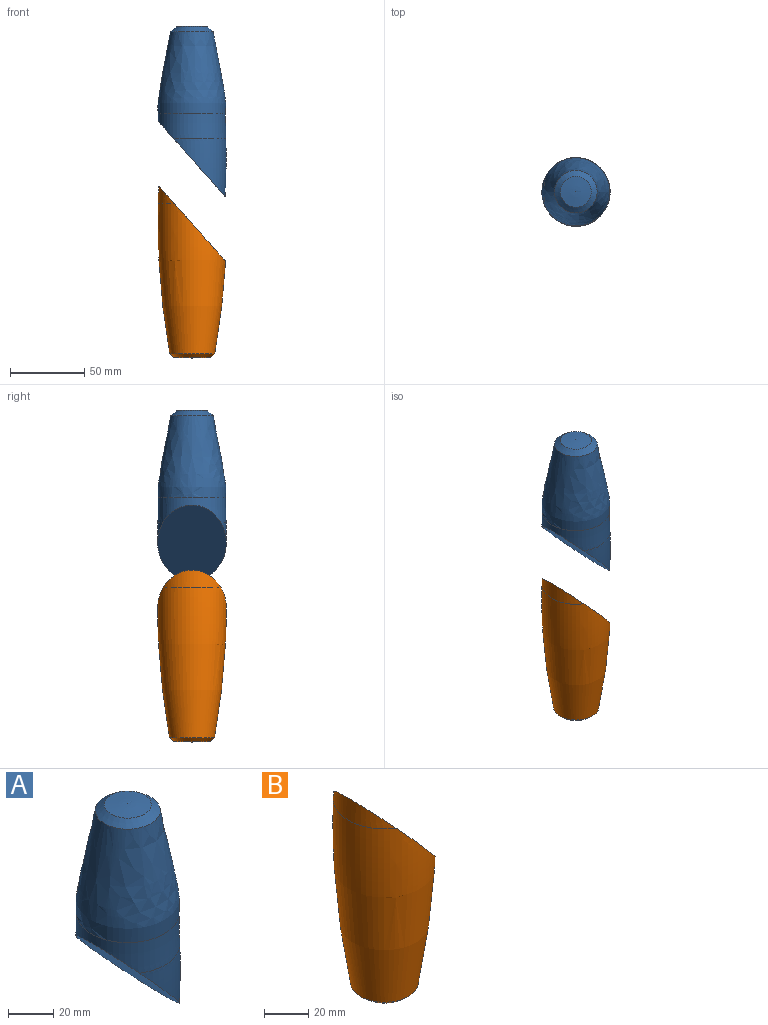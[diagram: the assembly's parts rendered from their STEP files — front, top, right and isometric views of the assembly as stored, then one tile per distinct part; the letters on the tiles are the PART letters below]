
ASSEMBLY  parts=2 mates=1
PART A: 6 faces, bbox 46.1x46.4x115.1 mm
  f0: revolved ~46.35x39.05mm, area 2344.6mm2, adj f1,f5
  f1: revolved ~45.49x45.49mm, area 4454.2mm2, adj f0,f2,f5
  f2: revolved ~55.52x45.88mm, area 6849.8mm2, adj f1,f3
  f3: cone r=14.37mm half-angle=51.3deg, axis (0,0,-1), area 394.4mm2, adj f2,f4
  f4: revolved ~20.83x20.83mm, area 341.6mm2, adj f3
  f5: plane 50.96x46.37mm, normal (-0.75,0,-0.66), area 2478mm2, adj f0,f1
PART B: 5 faces, bbox 46.3x46.4x116.1 mm
  f0: plane 50.96x46.37mm, normal (0.75,0,0.66), area 2478mm2, adj f3,f4
  f1: revolved ~24.84x24.84mm, area 485.6mm2, adj f2
  f2: cone r=12.42mm half-angle=49.2deg, axis (0,0,1), area 318.9mm2, adj f1,f4
  f3: revolved ~39.17x11.9mm, area 363.2mm2, adj f0,f4
  f4: revolved ~101.24x46.33mm, area 10962.1mm2, adj f0,f2,f3
PLACE A t=(-22.32,20.65,86.73)mm
PLACE B t=(-22.05,20.62,42.85)mm
MATE parallel A.f5 <-> B.f0  axis (-0.75,0,-0.66) through (-69.53,20.65,47.42)mm
